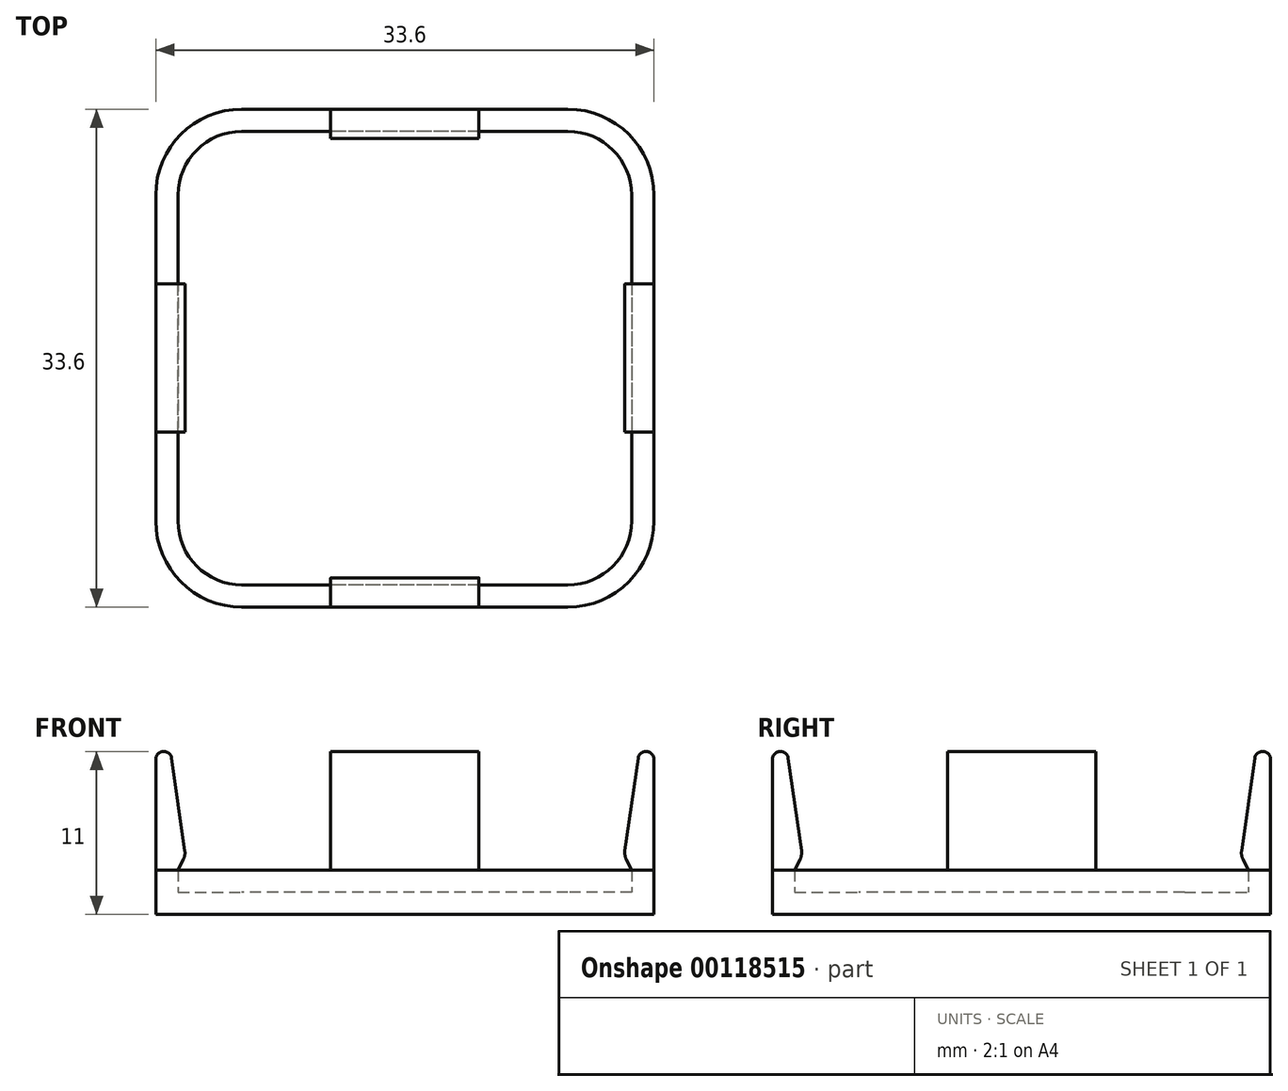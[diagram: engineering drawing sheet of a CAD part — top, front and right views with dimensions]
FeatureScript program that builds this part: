
annotation { "Feature Type Name" : "Feature", "Feature Type Description" : "" }
export const myFeature = defineFeature(function(context is Context, id is Id, definition is map)
    precondition{}
    {
        {
            var Q0;
            Q0=qCreatedBy(makeId("Top.planeOp"),FACE);
            var sketch = newSketch(context, id + "F0", { "sketchPlane" : qUnion([Q0])});
            skLineSegment(sketch, "E0.bottom", {"start": v(11, 15) * mm, "end": v(-11, 15) * mm});
            skLineSegment(sketch, "E0.top", {"start": v(11, -15) * mm, "end": v(-11, -15) * mm});
            skLineSegment(sketch, "E0.left", {"start": v(15, 11) * mm, "end": v(15, -11) * mm});
            skLineSegment(sketch, "E0.right", {"start": v(-15, 11) * mm, "end": v(-15, -11) * mm});
            skPoint(sketch, "E0.middle", {"position": v(0, 0) * mm});
            skPoint(sketch, "E1.visualSharp", {"position": v(15, 15) * mm});
            skArc(sketch, "E1.filletArc", {"start": v(15, 11) * mm, "mid": v(13.83, 13.83) * mm, "end": v(11, 15) * mm});
            skPoint(sketch, "E2.visualSharp", {"position": v(15, -15) * mm});
            skArc(sketch, "E2.filletArc", {"start": v(11, -15) * mm, "mid": v(13.83, -13.83) * mm, "end": v(15, -11) * mm});
            skPoint(sketch, "E3.visualSharp", {"position": v(-15, -15) * mm});
            skArc(sketch, "E3.filletArc", {"start": v(-15, -11) * mm, "mid": v(-13.83, -13.83) * mm, "end": v(-11, -15) * mm});
            skPoint(sketch, "E4.visualSharp", {"position": v(-15, 15) * mm});
            skArc(sketch, "E4.filletArc", {"start": v(-11, 15) * mm, "mid": v(-13.83, 13.83) * mm, "end": v(-15, 11) * mm});
            skLineSegment(sketch, "E5.0", {"start": v(11, 15.3) * mm, "end": v(-11, 15.3) * mm});
            skArc(sketch, "E5.1", {"start": v(15.3, 11) * mm, "mid": v(14.04, 14.04) * mm, "end": v(11, 15.3) * mm});
            skArc(sketch, "E5.2", {"start": v(-11, 15.3) * mm, "mid": v(-14.04, 14.04) * mm, "end": v(-15.3, 11) * mm});
            skLineSegment(sketch, "E5.3", {"start": v(15.3, 11) * mm, "end": v(15.3, -11) * mm});
            skLineSegment(sketch, "E5.4", {"start": v(-15.3, 11) * mm, "end": v(-15.3, -11) * mm});
            skArc(sketch, "E5.5", {"start": v(-15.3, -11) * mm, "mid": v(-14.04, -14.04) * mm, "end": v(-11, -15.3) * mm});
            skLineSegment(sketch, "E5.6", {"start": v(11, -15.3) * mm, "end": v(-11, -15.3) * mm});
            skArc(sketch, "E5.7", {"start": v(11, -15.3) * mm, "mid": v(14.04, -14.04) * mm, "end": v(15.3, -11) * mm});
            skLineSegment(sketch, "E6.0", {"start": v(11, 16.8) * mm, "end": v(-11, 16.8) * mm});
            skArc(sketch, "E6.1", {"start": v(16.8, 11) * mm, "mid": v(15.1, 15.1) * mm, "end": v(11, 16.8) * mm});
            skArc(sketch, "E6.2", {"start": v(-11, 16.8) * mm, "mid": v(-15.1, 15.1) * mm, "end": v(-16.8, 11) * mm});
            skLineSegment(sketch, "E6.3", {"start": v(16.8, 11) * mm, "end": v(16.8, -11) * mm});
            skLineSegment(sketch, "E6.4", {"start": v(-16.8, 11) * mm, "end": v(-16.8, -11) * mm});
            skArc(sketch, "E6.5", {"start": v(-16.8, -11) * mm, "mid": v(-15.1, -15.1) * mm, "end": v(-11, -16.8) * mm});
            skLineSegment(sketch, "E6.6", {"start": v(11, -16.8) * mm, "end": v(-11, -16.8) * mm});
            skArc(sketch, "E6.7", {"start": v(11, -16.8) * mm, "mid": v(15.1, -15.1) * mm, "end": v(16.8, -11) * mm});
            skSolve(sketch);
        }
        {
            var Q0;
            Q0=makeQuery(id+"F0.imprint","IMPRINT",FACE,{"disambiguationData":[TD([[makeQuery(id+"F0.imprint","IMPRINT",EDGE,{"derivedFrom":sQuery(id+"F0.wireOp",EDGE,"E5.0")}),-1.0]])]});
            var Q1;
            Q1=makeQuery(id+"F0.imprint","IMPRINT",FACE,{"disambiguationData":[TD([[makeQuery(id+"F0.imprint","IMPRINT",EDGE,{"derivedFrom":sQuery(id+"F0.wireOp",EDGE,"E0.bottom")}),-1.0]])]});
            var Q2;
            Q2=makeQuery(id+"F0.imprint","IMPRINT",FACE,{"disambiguationData":[TD([[makeQuery(id+"F0.imprint","IMPRINT",EDGE,{"derivedFrom":sQuery(id+"F0.wireOp",EDGE,"E0.bottom")}),1.0]])]});
            extrude(context, id + "F1", {"entities" : qUnion([Q0, Q1, Q2]), "depth" : 1.5 * mm});
        }
        {
            var Q0;
            Q0=makeQuery(id+"F1.opExtrude","CAP_FACE",FACE,{"disambiguationData":[OSD([sQuery(id+"F0.wireOp",EDGE,"E6.0"),sQuery(id+"F0.wireOp",EDGE,"E6.1"),sQuery(id+"F0.wireOp",EDGE,"E6.2"),sQuery(id+"F0.wireOp",EDGE,"E6.3"),sQuery(id+"F0.wireOp",EDGE,"E6.4"),sQuery(id+"F0.wireOp",EDGE,"E6.5"),sQuery(id+"F0.wireOp",EDGE,"E6.6"),sQuery(id+"F0.wireOp",EDGE,"E6.7")])],"isStart":false});
            var sketch = newSketch(context, id + "F2", { "sketchPlane" : qUnion([Q0])});
            skLineSegment(sketch, "E7.0", {"start": v(11, 15.3) * mm, "end": v(-11, 15.3) * mm});
            skArc(sketch, "E7.1", {"start": v(15.3, 11) * mm, "mid": v(14.04, 14.04) * mm, "end": v(11, 15.3) * mm});
            skArc(sketch, "E7.2", {"start": v(-11, 15.3) * mm, "mid": v(-14.04, 14.04) * mm, "end": v(-15.3, 11) * mm});
            skLineSegment(sketch, "E7.3", {"start": v(15.3, 11) * mm, "end": v(15.3, -11) * mm});
            skLineSegment(sketch, "E7.4", {"start": v(-15.3, 11) * mm, "end": v(-15.3, -11) * mm});
            skArc(sketch, "E7.5", {"start": v(-15.3, -11) * mm, "mid": v(-14.04, -14.04) * mm, "end": v(-11, -15.3) * mm});
            skLineSegment(sketch, "E7.6", {"start": v(11, -15.3) * mm, "end": v(-11, -15.3) * mm});
            skArc(sketch, "E7.7", {"start": v(11, -15.3) * mm, "mid": v(14.04, -14.04) * mm, "end": v(15.3, -11) * mm});
            skSolve(sketch);
        }
        {
            var Q0;
            Q0=makeQuery(id+"F2.imprint","IMPRINT",FACE,{"disambiguationData":[TD([[makeQuery(id+"F2.imprint","IMPRINT",EDGE,{"derivedFrom":sQuery(id+"F2.wireOp",EDGE,"E7.0")}),-1.0]])]});
            extrude(context, id + "F3", {"entities" : qUnion([Q0]), "operationType" : NewBodyOperationType.ADD, "depth" : 1.5 * mm});
        }
        {
            var Q0;
            Q0=qCreatedBy(makeId("Front.planeOp"),FACE);
            var sketch = newSketch(context, id + "F4", { "sketchPlane" : qUnion([Q0])});
            skLineSegment(sketch, "E8", {"start": v(0, 0) * mm, "end": v(-16.8, 0) * mm, "construction": true});
            skLineSegment(sketch, "E9", {"start": v(-16.8, 3) * mm, "end": v(-16.8, 10.5) * mm});
            skLineSegment(sketch, "E10.0", {"start": v(0, 3) * mm, "end": v(-16.8, 3) * mm, "construction": true});
            skLineSegment(sketch, "E11.0", {"start": v(-15.8, 3) * mm, "end": v(-15.8, 11) * mm});
            skLineSegment(sketch, "E12.0", {"start": v(-14.8, 3) * mm, "end": v(-14.8, 11) * mm});
            skLineSegment(sketch, "E13.0", {"start": v(-15.3, 3) * mm, "end": v(-15.3, 11) * mm});
            skLineSegment(sketch, "E14.0", {"start": v(0, 4) * mm, "end": v(-16.8, 4) * mm});
            skLineSegment(sketch, "E15", {"start": v(-15.3, 3) * mm, "end": v(-14.94, 3.72) * mm});
            skLineSegment(sketch, "E16", {"start": v(-14.84, 4.3) * mm, "end": v(-15.74, 10.57) * mm});
            skLineSegment(sketch, "E17", {"start": v(-16.23, 11) * mm, "end": v(-16.3, 11) * mm});
            skPoint(sketch, "E18.visualSharp", {"position": v(-16.8, 11) * mm});
            skArc(sketch, "E18.filletArc", {"start": v(-16.3, 11) * mm, "mid": v(-16.65, 10.85) * mm, "end": v(-16.8, 10.5) * mm});
            skPoint(sketch, "E19.visualSharp", {"position": v(-15.8, 11) * mm});
            skArc(sketch, "E19.filletArc", {"start": v(-15.74, 10.57) * mm, "mid": v(-15.9, 10.88) * mm, "end": v(-16.23, 11) * mm});
            skPoint(sketch, "E20.visualSharp", {"position": v(-14.8, 4) * mm});
            skArc(sketch, "E20.filletArc", {"start": v(-14.94, 3.72) * mm, "mid": v(-14.85, 4) * mm, "end": v(-14.84, 4.3) * mm});
            skLineSegment(sketch, "E21", {"start": v(-15.3, 3) * mm, "end": v(-16.8, 3) * mm});
            skLineSegment(sketch, "E22", {"start": v(0, 0) * mm, "end": v(0, 33.18) * mm, "construction": true});
            skSolve(sketch);
        }
        {
            var Q0;
            {var subQ0=sQuery(id+"F4.wireOp",EDGE,"E17");Q0=makeQuery(id+"F4.imprint","IMPRINT",FACE,{"disambiguationData":[TD([[makeQuery(id+"F4.imprint","IMPRINT",EDGE,{"derivedFrom":subQ0}),1.0]])]});}
            var Q1;
            {var subQ0=sQuery(id+"F4.wireOp",EDGE,"E21");var subQ1=sQuery(id+"F4.wireOp",EDGE,"E9");var subQ2=makeQuery(id+"F4.imprint","INTERSECT",VERTEX,{"derivedFrom":[subQ1,subQ0]});Q1=makeQuery(id+"F4.imprint","IMPRINT",FACE,{"disambiguationData":[TD([[makeQuery(id+"F4.imprint","IMPRINT",EDGE,{"disambiguationData":[TD([[subQ2,-1.0]])],"derivedFrom":subQ1}),-1.0]])]});}
            var Q2;
            {var subQ0=sQuery(id+"F4.wireOp",EDGE,"E21");var subQ1=sQuery(id+"F4.wireOp",EDGE,"E11.0");var subQ2=makeQuery(id+"F4.imprint","INTERSECT",VERTEX,{"derivedFrom":[subQ1,subQ0]});Q2=makeQuery(id+"F4.imprint","IMPRINT",FACE,{"disambiguationData":[TD([[makeQuery(id+"F4.imprint","IMPRINT",EDGE,{"disambiguationData":[TD([[subQ2,-1.0]])],"derivedFrom":subQ1}),-1.0]])]});}
            var Q3;
            {var subQ0=sQuery(id+"F4.wireOp",EDGE,"E19.filletArc");var subQ5=sQuery(id+"F4.wireOp",EDGE,"E11.0");var subQ6=makeQuery(id+"F4.imprint","INTERSECT",VERTEX,{"derivedFrom":[subQ5,subQ0]});Q3=makeQuery(id+"F4.imprint","IMPRINT",FACE,{"disambiguationData":[TD([[makeQuery(id+"F4.imprint","IMPRINT",EDGE,{"disambiguationData":[TD([[subQ6,1.0]])],"derivedFrom":subQ5}),-1.0]])]});}
            var Q4;
            {var subQ0=sQuery(id+"F4.wireOp",EDGE,"E16");var subQ1=sQuery(id+"F4.wireOp",EDGE,"E13.0");var subQ2=makeQuery(id+"F4.imprint","INTERSECT",VERTEX,{"derivedFrom":[subQ1,subQ0]});Q4=makeQuery(id+"F4.imprint","IMPRINT",FACE,{"disambiguationData":[TD([[makeQuery(id+"F4.imprint","IMPRINT",EDGE,{"disambiguationData":[TD([[subQ2,1.0]])],"derivedFrom":subQ1}),-1.0]])]});}
            var Q5;
            {var subQ0=sQuery(id+"F4.wireOp",EDGE,"E15");Q5=makeQuery(id+"F4.imprint","IMPRINT",FACE,{"disambiguationData":[TD([[makeQuery(id+"F4.imprint","IMPRINT",EDGE,{"derivedFrom":subQ0}),1.0]])]});}
            extrude(context, id + "F5", {"entities" : qUnion([Q0, Q1, Q2, Q3, Q4, Q5]), "depth" : 5 * mm, "hasSecondDirection" : true, "secondDirectionOppositeDirection" : true, "secondDirectionDepth" : 5 * mm});
        }
        {
            var Q0;
            Q0=makeQuery(id+"F5.opExtrude","SWEPT_BODY",BODY,{"disambiguationData":[OSD([sQuery(id+"F4.wireOp",EDGE,"E9"),sQuery(id+"F4.wireOp",EDGE,"E15"),sQuery(id+"F4.wireOp",EDGE,"E16"),sQuery(id+"F4.wireOp",EDGE,"E17"),sQuery(id+"F4.wireOp",EDGE,"E18.filletArc"),sQuery(id+"F4.wireOp",EDGE,"E19.filletArc"),sQuery(id+"F4.wireOp",EDGE,"E20.filletArc"),sQuery(id+"F4.wireOp",EDGE,"E21")])]});
            var Q1;
            Q1=sQuery(id+"F4.wireOp",EDGE,"E22");
            circularPattern(context, id + "F6", {"entities" : qUnion([Q0]), "axis" : qUnion([Q1]), "angle" : 90 * degree, "instanceCount" : 4});
        }
    });
